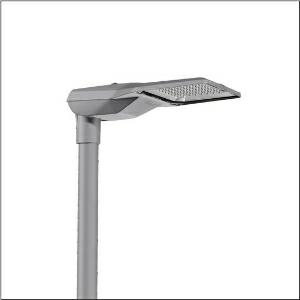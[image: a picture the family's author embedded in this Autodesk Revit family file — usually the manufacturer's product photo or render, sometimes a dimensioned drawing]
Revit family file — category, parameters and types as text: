
# Revit family: streetlight_sl_21_midi___st1_0a_5xe3d43s08mb_8ac5
name_source: partatom
category: Lighting Fixtures
units: mm (PartAtom-declared; Revit-internal decimal feet)

## family parameters
Cut with Voids When Loaded = No
Host = Face
Light Source = No
Part Type = Normal
Room Calculation Point = No
Round Connector Dimension = Use Diameter
Shared = No

## types (1)
- --- (1 x LED, 20180 lm, 147 W, 4000K)
    Apparent Load = 147 VA
    CIE Flux Codes = 37 72 97 100 100
    Color Rendering = 70
    Color Temperature = 4000K
    Default Elevation = 1800 mm
    Description = Streetlight SL 21 midi, mast luminaire, primary light control with lens, of PMMA, primary optical cover: cover, of toughened safety glass, transparent, light distribution: ST1.0a, light emission: direct distribution, primary light characteristic: asymmetric, installation type: side-entry, post-top, LED, High Power LED, rated luminous flux: 20.180lm, luminous efficacy: 137lm/W, light colour: 740, colour temperature: 4000K, control gear: D4i, control: overheat protection, constant luminous flux control, time-dependent luminous flux control, flexible luminous flux parameterisation, pre-setting: logarithmic dimming characteristic, mains connection: 230..240V, AC, 50/60Hz, start of lifetime: 147W, end of service life: 155W, reduction: 65W, luminaire housing, of diecast aluminium, powder-coated, SITECO metallic grey (DB 702S), corrosivity category C5 high according to DIN EN ISO 12944, please order mast flange separately, inclination adjustable: 0°, 5°, 10°, 15°, sealing non-destructively replaceable, multi-level sealing system, length: 644mm, width: 335mm, height: 110mm, mast flange for spigot size: 42mm (side-entry): 5XC10008XM4, 60/48mm (side-entry/post-top): 5XC10108XM2, 76/60mm (side-entry/post-top): 5XC10108XM1, mounting height: 4..8m, Smart Interface above, protection rating (complete): IP66, insulation class (complete): insulation class II (safety insulation), certification: CE, ENEC, ENEC+, VDE, impact resistance: IK10, permissible operating ambient temperature for outdoor applications: -40..+50°C, standard-compliant lighting for roads and squares, packaging unit: 1 piece

Light Distribution: ST1.0a
    Height = 111 mm
    Lamp = 1 x LED
    Lamp Light Flux = 20180 lm
    Lamp Power = 147 W
    Lamp count = 1
    Length = 644 mm
    Luminous efficacy = 137 lm/W
    Manufacturer = Siteco
    ModVariant = No
    Model = 5XE3D43S08MB
    Number of Poles = 1
    OnlyDefault = Yes
    Power Factor = 1
    Product Name = Streetlight SL 21 midi | ST1.0a
    Product group = mast luminaire | pylon top
    ProductGroupID = 6100
    Protection Class = Protection class II
    Protection Degree = IP 66
    RLX_Detail_Level = 1
    RLX_Emergency_Light_Flux = 0 lm
    RLX_Emergency_Type = 0
    RLX_Emergency_Type_DB = No
    RlxData = <blob elided: 26825 chars, md5=e4ae764e>
    Socket = socket
    Standby Power = 0 W
    System Light Flux = 20180 lm
    System Power = 147 W
    Type Comments = factory setting: luminous flux: 100 % | dim-lin: 254 | 750 mA
    Type Image = l_1004302.jpg
    URL = http://relux.com
    VarID = @adj_186769
    Voltage = 0 V
    Weight = 0.00 kg
    Width = 336 mm

## geometry (parser evidence)
native form markers: Blend x4, Sweep x11
no freeform markers — native parametric forms only
